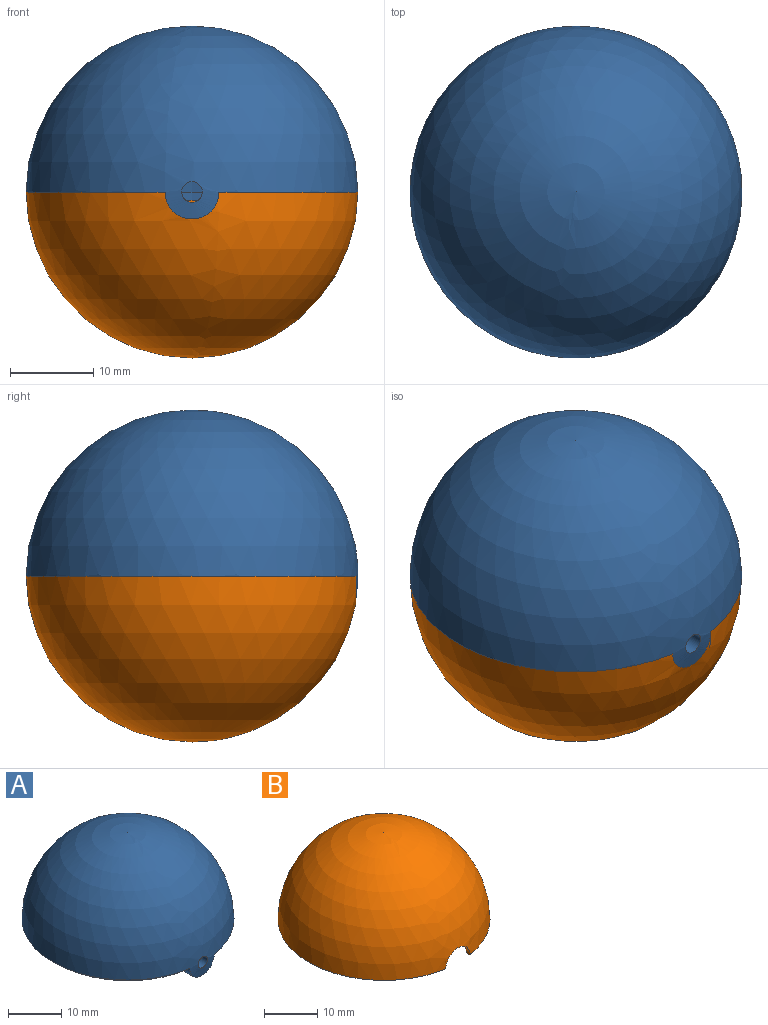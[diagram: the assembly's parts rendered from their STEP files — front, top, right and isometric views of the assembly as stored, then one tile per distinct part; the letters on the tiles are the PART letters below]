
ASSEMBLY  parts=2 mates=1
PART A: 9 faces, bbox 40x40x23.3 mm
  f0: sphere r=20mm, area 2525.1mm2, adj f1,f6,f8
  f1: plane 40x39.73mm, normal (0,0,-1), area 138.4mm2, adj f0,f2,f6
  f2: cylinder r=18.8mm len=37.6mm, axis (0,0,-1), area 111.7mm2, adj f1,f3,f6
  f3: plane 37.6x37.34mm, normal (0,0,-1), area 87.5mm2, adj f2,f4,f6
  f4: cylinder r=18mm len=36mm, axis (0,0,-1), area 106.7mm2, adj f3,f5,f6
  f5: sphere r=18mm, area 2019mm2, adj f4,f6
  f6: cylinder r=3.25mm len=9.73mm, axis (0,1,0), area 176.4mm2, adj f0,f1,f2,f3,f4,f5,f7
  f7: plane 6.5x6.5mm, normal (0,1,0), area 28.3mm2, adj f6,f8
  f8: cylinder r=1.25mm len=9.96mm, axis (0,1,0), area 78.2mm2, adj f0,f7
PART B: 6 faces, bbox 40x40x20 mm
  f0: plane 40x39.73mm, normal (0,0,-1), area 116mm2, adj f1,f4,f5
  f1: cylinder r=19mm len=38mm, axis (0,0,-1), area 226.6mm2, adj f0,f2,f5
  f2: plane 38x37.83mm, normal (0,0,-1), area 123.1mm2, adj f1,f3,f5
  f3: sphere r=18mm, area 1805mm2, adj f2,f5
  f4: sphere r=20mm, area 2496.6mm2, adj f0,f5
  f5: cylinder r=3.25mm len=6.5mm, axis (0,1,0), area 16.2mm2, adj f0,f1,f2,f3,f4
PLACE A t=(7.39,-15.47,0)mm
PLACE B rot(axis=(0,1,0),180deg) t=(7.39,-15.47,0)mm
MATE ball B.f1 <-> A.f2  axis (0,0,1) through (7.39,-15.47,0)mm
